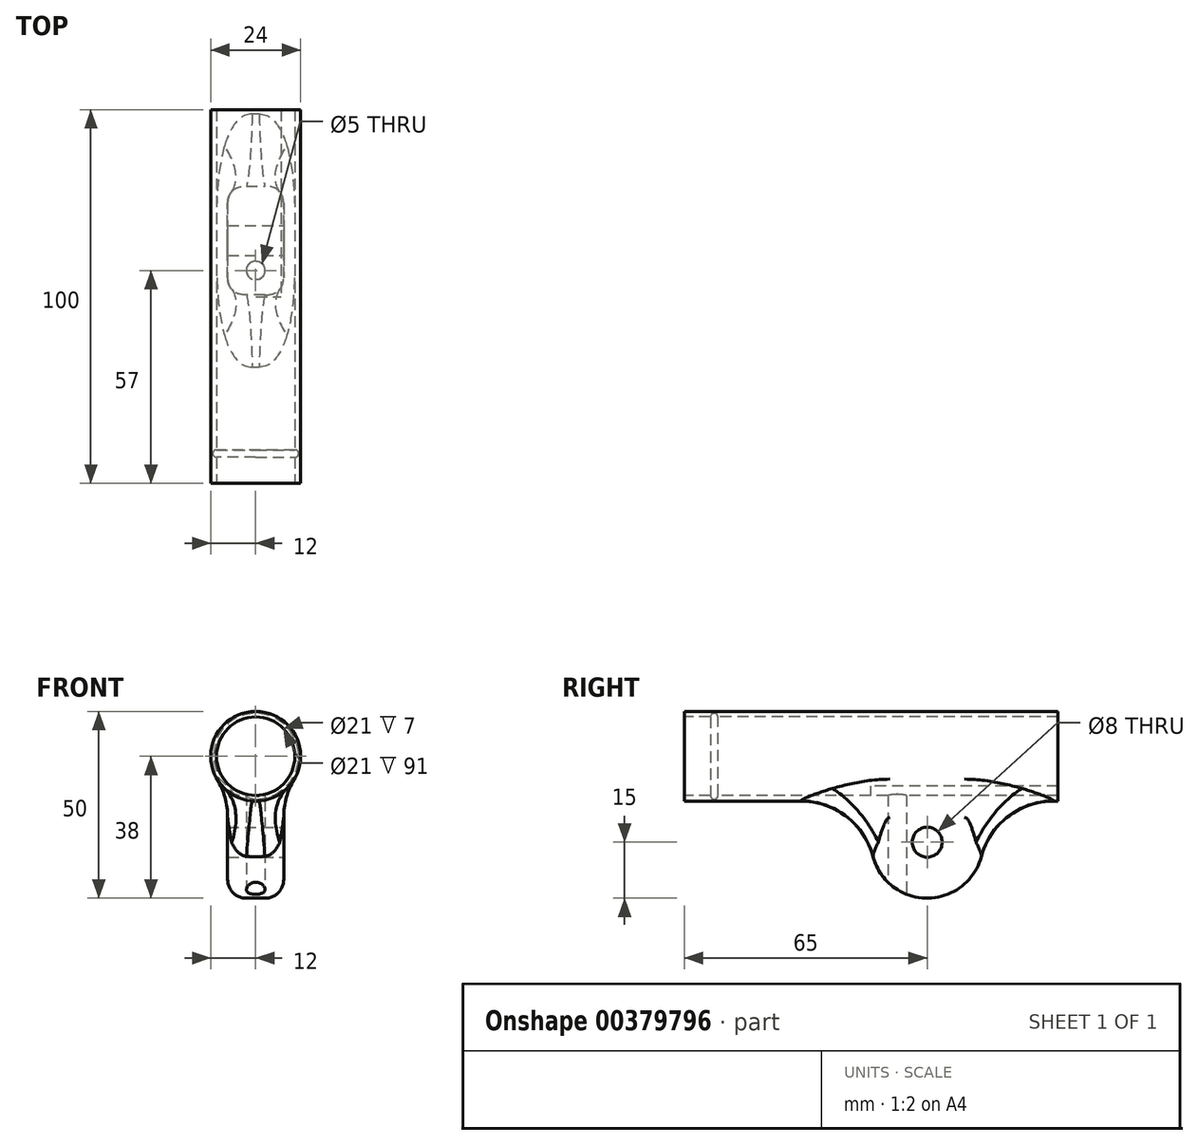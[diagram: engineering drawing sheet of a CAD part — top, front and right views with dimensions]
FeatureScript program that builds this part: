
annotation { "Feature Type Name" : "Feature", "Feature Type Description" : "" }
export const myFeature = defineFeature(function(context is Context, id is Id, definition is map)
    precondition{}
    {
        {
            var Q0;
            Q0=qCreatedBy(makeId("Front.planeOp"),FACE);
            var sketch = newSketch(context, id + "F0", { "sketchPlane" : qUnion([Q0])});
            skLineSegment(sketch, "E0.bottom", {"start": v(0, 0) * mm, "end": v(15, 0) * mm});
            skLineSegment(sketch, "E0.top", {"start": v(0, 30) * mm, "end": v(15, 30) * mm});
            skLineSegment(sketch, "E0.left", {"start": v(0, 0) * mm, "end": v(0, 30) * mm});
            skLineSegment(sketch, "E0.right", {"start": v(15, 0) * mm, "end": v(15, 30) * mm});
            skSolve(sketch);
        }
        {
            var Q0;
            Q0 = qSketchRegion(id + "F0", true);
            extrude(context, id + "F1", {"entities" : qUnion([Q0]), "depth" : 30 * mm});
        }
        {
            var Q0;
            Q0=makeQuery(id+"F1.opExtrude","SWEPT_FACE",FACE,{"disambiguationData":[OSD([sQuery(id+"F0.wireOp",EDGE,"E0.right")])]});
            var sketch = newSketch(context, id + "F2", { "sketchPlane" : qUnion([Q0])});
            skCircle(sketch, "E1", {"center": v(-15, 15) * mm, "radius": 4 * mm});
            skPoint(sketch, "E1.centerSnap0", {"position": v(-30, 15) * mm});
            skPoint(sketch, "E1.centerSnap1", {"position": v(-15, 30) * mm});
            skSolve(sketch);
        }
        {
            var Q0;
            Q0 = qSketchRegion(id + "F2", true);
            extrude(context, id + "F3", {"entities" : qUnion([Q0]), "operationType" : NewBodyOperationType.REMOVE, "endBound" : BoundingType.THROUGH_ALL, "oppositeDirection" : true, "depth" : 25 * mm});
        }
        {
            var Q0;
            Q0=makeQuery(id+"F1.opExtrude","CAP_FACE",FACE,{"disambiguationData":[OSD([sQuery(id+"F0.wireOp",EDGE,"E0.bottom"),sQuery(id+"F0.wireOp",EDGE,"E0.top"),sQuery(id+"F0.wireOp",EDGE,"E0.left"),sQuery(id+"F0.wireOp",EDGE,"E0.right")])],"isStart":false});
            var sketch = newSketch(context, id + "F4", { "sketchPlane" : qUnion([Q0])});
            skCircle(sketch, "E2", {"center": v(7.5, 38) * mm, "radius": 12 * mm});
            skPoint(sketch, "E2.centerSnap0", {"position": v(7.5, 30) * mm});
            skSolve(sketch);
        }
        {
            var Q0;
            Q0 = qSketchRegion(id + "F4", true);
            extrude(context, id + "F5", {"entities" : qUnion([Q0]), "endBound" : BoundingType.SYMMETRIC, "depth" : 100 * mm});
        }
        {
            var Q0;
            Q0=makeQuery(id+"F5.opExtrude","CAP_FACE",FACE,{"disambiguationData":[OSD([sQuery(id+"F4.wireOp",EDGE,"E2")])],"isStart":false});
            var sketch = newSketch(context, id + "F6", { "sketchPlane" : qUnion([Q0])});
            skCircle(sketch, "E3", {"center": v(7.5, 38) * mm, "radius": 10.5 * mm});
            skSolve(sketch);
        }
        {
            var Q0;
            Q0 = qSketchRegion(id + "F6", true);
            extrude(context, id + "F7", {"entities" : qUnion([Q0]), "operationType" : NewBodyOperationType.REMOVE, "endBound" : BoundingType.THROUGH_ALL, "oppositeDirection" : true, "depth" : 25 * mm});
        }
        {
            var Q0;
            Q0=makeQuery(id+"F1.opExtrude","CAP_FACE",FACE,{"disambiguationData":[OSD([sQuery(id+"F0.wireOp",EDGE,"E0.bottom"),sQuery(id+"F0.wireOp",EDGE,"E0.top"),sQuery(id+"F0.wireOp",EDGE,"E0.left"),sQuery(id+"F0.wireOp",EDGE,"E0.right")])],"isStart":false});
            var sketch = newSketch(context, id + "F8", { "sketchPlane" : qUnion([Q0])});
            skPoint(sketch, "E4.centerSnap0", {"position": v(7.5, 30) * mm});
            skArc(sketch, "E5", {"start": v(0.76, 30) * mm, "mid": v(7.55, 27.5) * mm, "end": v(14.33, 30) * mm});
            skLineSegment(sketch, "E6", {"start": v(0.76, 30) * mm, "end": v(7.36, 32.98) * mm});
            skLineSegment(sketch, "E7", {"start": v(7.36, 32.98) * mm, "end": v(14.33, 30) * mm});
            skPoint(sketch, "E4.center.orphan", {"position": v(7.5, 38) * mm});
            skSolve(sketch);
        }
        {
            var Q0;
            Q0=makeQuery(id+"F1.opExtrude","CAP_EDGE",EDGE,{"disambiguationData":[OSD([sQuery(id+"F0.wireOp",EDGE,"E0.bottom")])],"isStart":false});
            var Q1;
            Q1=makeQuery(id+"F1.opExtrude","CAP_EDGE",EDGE,{"disambiguationData":[OSD([sQuery(id+"F0.wireOp",EDGE,"E0.bottom")])],"isStart":true});
            fillet(context, id + "F9", {"entities" : qUnion([Q0, Q1]), "radius" : 15 * mm, "tangentPropagation" : true, "allowEdgeOverflow" : false});
        }
        {
            var Q0;
            Q0=makeQuery(id+"F1.opExtrude","CAP_EDGE",EDGE,{"disambiguationData":[OSD([sQuery(id+"F0.wireOp",EDGE,"E0.right")])],"isStart":false});
            var Q1;
            Q1=makeQuery(id+"F1.opExtrude","CAP_EDGE",EDGE,{"disambiguationData":[OSD([sQuery(id+"F0.wireOp",EDGE,"E0.left")])],"isStart":false});
            fillet(context, id + "F10", {"entities" : qUnion([Q0, Q1]), "radius" : 5 * mm, "tangentPropagation" : true, "allowEdgeOverflow" : false});
        }
        {
            var Q0;
            Q0=qCreatedBy(makeId("Top.planeOp"),FACE);
            var sketch = newSketch(context, id + "F11", { "sketchPlane" : qUnion([Q0])});
            skCircle(sketch, "E8", {"center": v(7.5, -23) * mm, "radius": 2.5 * mm});
            skSolve(sketch);
        }
        {
            var Q0;
            Q0=makeQuery(id+"F5.opExtrude","SWEPT_BODY",BODY,{"disambiguationData":[OSD([sQuery(id+"F4.wireOp",EDGE,"E2")])]});
            var Q1;
            Q1=makeQuery(id+"F1.opExtrude","SWEPT_BODY",BODY,{"disambiguationData":[OSD([sQuery(id+"F0.wireOp",EDGE,"E0.bottom"),sQuery(id+"F0.wireOp",EDGE,"E0.top"),sQuery(id+"F0.wireOp",EDGE,"E0.left"),sQuery(id+"F0.wireOp",EDGE,"E0.right")])]});
            booleanBodies(context, id + "F12", {"operationType" : BooleanOperationType.UNION, "tools" : qUnion([Q0, Q1])});
        }
        {
            var Q0;
            Q0=makeQuery(id+"F12.opBoolean","INTERSECT",EDGE,{"derivedFrom":[makeQuery(id+"F5.opExtrude","SWEPT_FACE",FACE,{"disambiguationData":[OSD([sQuery(id+"F4.wireOp",EDGE,"E2")])]}),makeQuery(id+"F1.opExtrude","SWEPT_FACE",FACE,{"disambiguationData":[OSD([sQuery(id+"F0.wireOp",EDGE,"E0.left")])]})]});
            fillet(context, id + "F13", {"entities" : qUnion([Q0]), "radius" : 20 * mm, "tangentPropagation" : true, "allowEdgeOverflow" : false});
        }
        {
            var Q0;
            Q0 = qSketchRegion(id + "F11", true);
            extrude(context, id + "F14", {"entities" : qUnion([Q0]), "operationType" : NewBodyOperationType.REMOVE, "depth" : 38.2 * mm});
        }
        {
            var Q0;
            Q0=qCreatedBy(makeId("Front.planeOp"),FACE);
            var sketch = newSketch(context, id + "F15", { "sketchPlane" : qUnion([Q0])});
            skLineSegment(sketch, "E9.bottom", {"start": v(7.5, 0) * mm, "end": v(28, 0) * mm});
            skLineSegment(sketch, "E9.top", {"start": v(7.5, 61.35) * mm, "end": v(28, 61.35) * mm});
            skLineSegment(sketch, "E9.left", {"start": v(7.5, 0) * mm, "end": v(7.5, 61.35) * mm});
            skLineSegment(sketch, "E9.right", {"start": v(28, 0) * mm, "end": v(28, 61.35) * mm});
            skSolve(sketch);
        }
        {
            var Q0;
            Q0 = qSketchRegion(id + "F15", true);
            extrude(context, id + "F16", {"entities" : qUnion([Q0]), "operationType" : NewBodyOperationType.REMOVE, "endBound" : BoundingType.SYMMETRIC, "oppositeDirection" : true, "depth" : 300 * mm});
        }
        {
            var Q0;
            Q0=makeQuery(id+"F16.boolean.opBoolean","COPY",FACE,{"disambiguationData":[TD([makeQuery(id+"F3.boolean.opBoolean","COPY",FACE,{"derivedFrom":makeQuery(id+"F3.opExtrude","SWEPT_FACE",FACE,{"disambiguationData":[OSD([sQuery(id+"F2.wireOp",EDGE,"E1")])]})})])],"derivedFrom":makeQuery(id+"F16.opExtrude","SWEPT_FACE",FACE,{"disambiguationData":[OSD([sQuery(id+"F15.wireOp",EDGE,"E9.left")])]})});
            var sketch = newSketch(context, id + "F17", { "sketchPlane" : qUnion([Q0])});
            skArc(sketch, "E10", {"start": v(7, 28.5) * mm, "mid": v(8, 27.5) * mm, "end": v(9, 28.5) * mm});
            skArc(sketch, "E11", {"start": v(-73, 27.55) * mm, "mid": v(-72, 26.5) * mm, "end": v(-71, 27.55) * mm});
            skLineSegment(sketch, "E12", {"start": v(-73, 27.55) * mm, "end": v(-71, 27.55) * mm});
            skLineSegment(sketch, "E13", {"start": v(7, 28.5) * mm, "end": v(9, 28.5) * mm});
            skSolve(sketch);
        }
        {
            var Q0;
            Q0=makeQuery(id+"F17.imprint","IMPRINT",FACE,{"disambiguationData":[TD([[makeQuery(id+"F17.imprint","IMPRINT",EDGE,{"derivedFrom":sQuery(id+"F17.wireOp",EDGE,"E11")}),1.0]])]});
            var Q1;
            Q1=makeQuery(id+"F17.imprint","IMPRINT",FACE,{"disambiguationData":[TD([[makeQuery(id+"F17.imprint","IMPRINT",EDGE,{"derivedFrom":sQuery(id+"F17.wireOp",EDGE,"E10")}),1.0]])]});
            var Q2;
            Q2=makeQuery(id+"F7.boolean.opBoolean","INTERSECT",EDGE,{"derivedFrom":[makeQuery(id+"F5.opExtrude","CAP_FACE",FACE,{"disambiguationData":[OSD([sQuery(id+"F4.wireOp",EDGE,"E2")])],"isStart":true}),makeQuery(id+"F7.opExtrude","SWEPT_FACE",FACE,{"disambiguationData":[OSD([sQuery(id+"F6.wireOp",EDGE,"E3")])]})]});
            sweep(context, id + "F18", {"operationType" : NewBodyOperationType.REMOVE, "profiles" : qUnion([Q0, Q1]), "path" : qUnion([Q2])});
        }
        {
            var Q0;
            Q0=makeQuery(id+"F5.opExtrude","SWEPT_BODY",BODY,{"disambiguationData":[OSD([sQuery(id+"F4.wireOp",EDGE,"E2")])]});
            var Q1;
            Q1=makeQuery(id+"F16.boolean.opBoolean","COPY",FACE,{"disambiguationData":[TD([makeQuery(id+"F3.boolean.opBoolean","COPY",FACE,{"derivedFrom":makeQuery(id+"F3.opExtrude","SWEPT_FACE",FACE,{"disambiguationData":[OSD([sQuery(id+"F2.wireOp",EDGE,"E1")])]})})])],"derivedFrom":makeQuery(id+"F16.opExtrude","SWEPT_FACE",FACE,{"disambiguationData":[OSD([sQuery(id+"F15.wireOp",EDGE,"E9.left")])]})});
            mirror(context, id + "F19", {"operationType" : NewBodyOperationType.ADD, "entities" : qUnion([Q0]), "mirrorPlane" : qUnion([Q1])});
        }
        {
            var Q0;
            Q0 = qSketchRegion(id + "F8", true);
            extrude(context, id + "F20", {"entities" : qUnion([Q0]), "operationType" : NewBodyOperationType.REMOVE, "endBound" : BoundingType.THROUGH_ALL, "oppositeDirection" : true, "depth" : 25 * mm, "offsetDistance" : 25 * mm});
        }
    });
